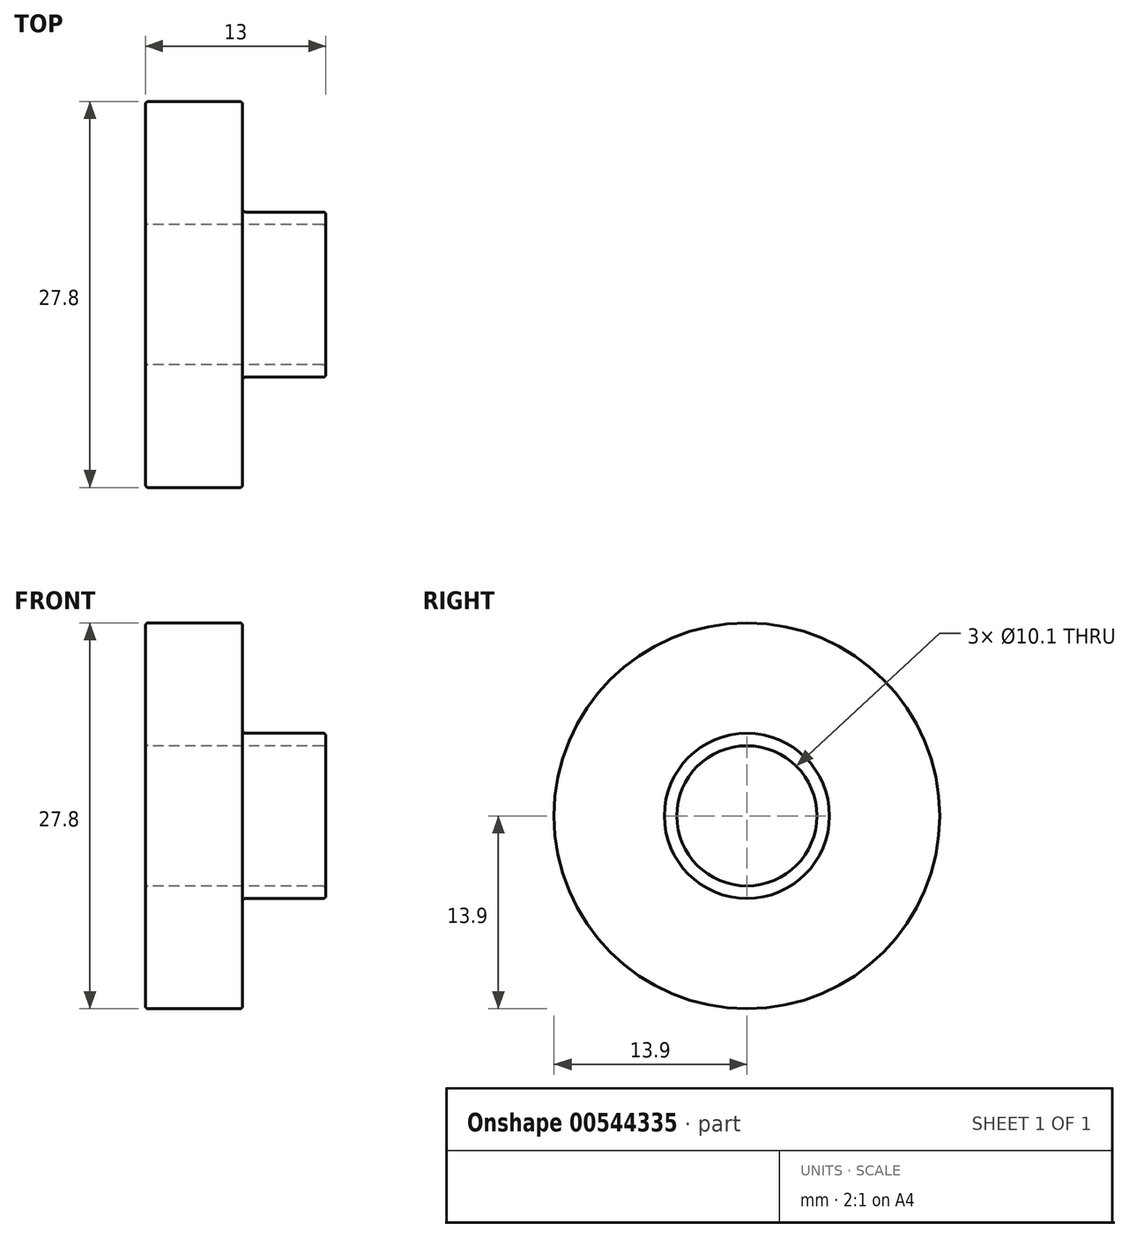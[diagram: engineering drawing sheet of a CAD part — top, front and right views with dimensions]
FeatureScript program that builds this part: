
annotation { "Feature Type Name" : "Feature", "Feature Type Description" : "" }
export const myFeature = defineFeature(function(context is Context, id is Id, definition is map)
    precondition{}
    {
        {
            var Q0;
            Q0=qCreatedBy(makeId("Front.planeOp"),FACE);
            var sketch = newSketch(context, id + "F0", { "sketchPlane" : qUnion([Q0])});
            skLineSegment(sketch, "E0", {"start": v(0, 5.05) * mm, "end": v(13, 5.05) * mm});
            skLineSegment(sketch, "E1", {"start": v(13, 5.05) * mm, "end": v(13, 5.95) * mm});
            skLineSegment(sketch, "E2", {"start": v(13, 5.95) * mm, "end": v(7, 5.95) * mm});
            skLineSegment(sketch, "E3", {"start": v(7, 5.95) * mm, "end": v(7, 13.9) * mm});
            skLineSegment(sketch, "E4", {"start": v(7, 13.9) * mm, "end": v(0, 13.9) * mm});
            skLineSegment(sketch, "E5", {"start": v(0, 13.9) * mm, "end": v(0, 5.05) * mm});
            skLineSegment(sketch, "E6", {"start": v(0, 0) * mm, "end": v(46.4, 0) * mm, "construction": true});
            skSolve(sketch);
        }
        {
            var Q0;
            Q0=makeQuery(id+"F0.imprint","IMPRINT",FACE,{"disambiguationData":[TD([[makeQuery(id+"F0.imprint","IMPRINT",EDGE,{"derivedFrom":sQuery(id+"F0.wireOp",EDGE,"E0")}),1.0]])]});
            var Q1;
            Q1=sQuery(id+"F0.wireOp",EDGE,"E6");
            revolve(context, id + "F1", {"entities" : qUnion([Q0]), "axis" : qUnion([Q1]), "revolveType" : RevolveType.FULL});
        }
        {
            var Q0;
            Q0=makeQuery(id+"F1.opRevolve","SWEPT_EDGE",EDGE,{"disambiguationData":[OSD([sQuery(id+"F0.wireOp",EDGE,"E2"),sQuery(id+"F0.wireOp",EDGE,"E3")])]});
            var Q1;
            Q1=makeQuery(id+"F1.opRevolve","SWEPT_EDGE",EDGE,{"disambiguationData":[OSD([sQuery(id+"F0.wireOp",EDGE,"E1"),sQuery(id+"F0.wireOp",EDGE,"E2")])]});
            var Q2;
            Q2=makeQuery(id+"F1.opRevolve","SWEPT_EDGE",EDGE,{"disambiguationData":[OSD([sQuery(id+"F0.wireOp",EDGE,"E0"),sQuery(id+"F0.wireOp",EDGE,"E1")])]});
            var Q3;
            Q3=makeQuery(id+"F1.opRevolve","SWEPT_EDGE",EDGE,{"disambiguationData":[OSD([sQuery(id+"F0.wireOp",EDGE,"E3"),sQuery(id+"F0.wireOp",EDGE,"E4")])]});
            var Q4;
            Q4=makeQuery(id+"F1.opRevolve","SWEPT_EDGE",EDGE,{"disambiguationData":[OSD([sQuery(id+"F0.wireOp",EDGE,"E4"),sQuery(id+"F0.wireOp",EDGE,"E5")])]});
            var Q5;
            Q5=makeQuery(id+"F1.opRevolve","SWEPT_EDGE",EDGE,{"disambiguationData":[OSD([sQuery(id+"F0.wireOp",EDGE,"E0"),sQuery(id+"F0.wireOp",EDGE,"E5")])]});
            fillet(context, id + "F2", {"entities" : qUnion([Q0, Q1, Q2, Q3, Q4, Q5]), "radius" : .2 * mm, "tangentPropagation" : true, "allowEdgeOverflow" : false});
        }
    });
